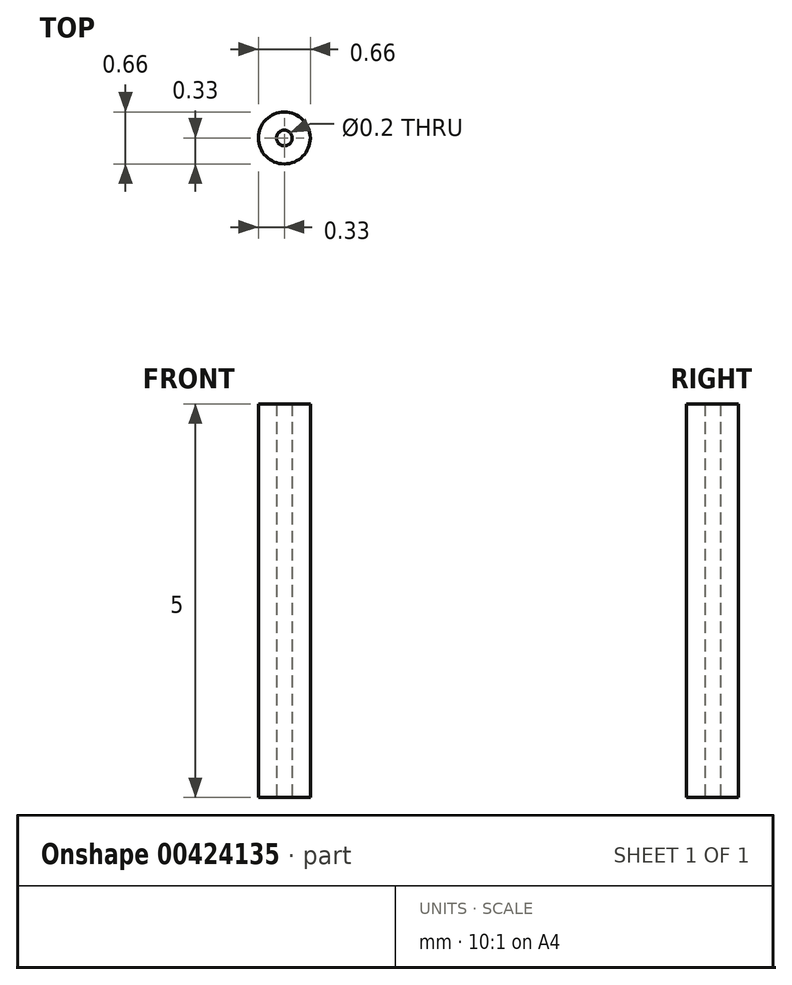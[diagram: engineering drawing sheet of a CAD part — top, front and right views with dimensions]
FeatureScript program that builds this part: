
annotation { "Feature Type Name" : "Feature", "Feature Type Description" : "" }
export const myFeature = defineFeature(function(context is Context, id is Id, definition is map)
    precondition{}
    {
        {
            var Q0;
            Q0=qCreatedBy(makeId("Top.planeOp"),FACE);
            var sketch = newSketch(context, id + "F0", { "sketchPlane" : qUnion([Q0])});
            skCircle(sketch, "E0", {"center": v(0, 0) * mm, "radius": 0.33 * mm});
            skCircle(sketch, "E1", {"center": v(0, 0) * mm, "radius": 0.1 * mm});
            skSolve(sketch);
        }
        {
            var Q0;
            Q0 = qSketchRegion(id + "F0", true);
            extrude(context, id + "F1", {"entities" : qUnion([Q0]), "depth" : 5 * mm});
        }
    });
